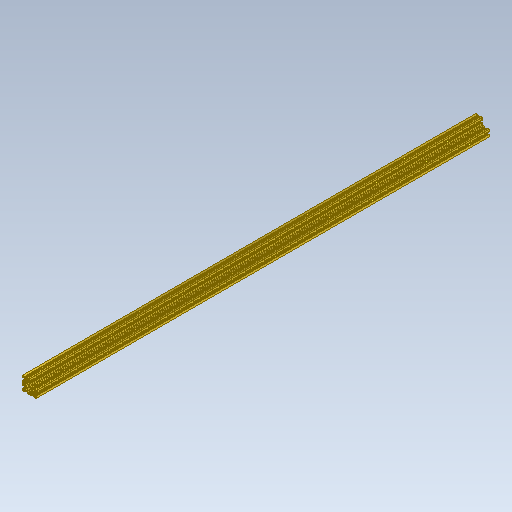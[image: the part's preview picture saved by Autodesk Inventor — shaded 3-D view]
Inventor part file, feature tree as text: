
AUTODESK INVENTOR PART (.ipt)
format: ipt  version: 2025.2 (Build 292293000, 293)  size: 549,376 bytes
history: native  units: mm
features: sketch x4, extrude x1, fillet x1
ambient origin geometry x8: Origin, YZ Plane, XZ Plane, XY Plane, X Axis, Y Axis, Z Axis, Center Point
bodies: Body1 (feature_tree)
feature tree (6):
  extrude  "Extrusão2"  Depth=10.0mm
  fillet  "Arredondamento1"  Radius=10.0mm
  sketch  "Esboço1"  dims[d0=60.0mm d3=15.0mm d4=10.0mm]
  sketch  "Esboço - Padrão circular1"  dims[d5=26.5mm]
  sketch  "Esboço - Padrão circular2"  dims[d7=4.5mm]
  sketch  "Esboço - Padrão circular3"  dims[d9=8.0mm d10=8.2mm d14=1.1mm d16=1.1mm d18=1.1mm d20=2.2mm d21=2.2mm d22=40.0mm d24=360.0deg d27=8.0mm d30=40.0mm d32=360.0deg d34=1.1mm d35=1.1mm d36=2.2mm d37=2.2mm d41=8.0mm d43=40.0mm d45=360.0deg d47=2000.0mm d48=0.0mm d49=1.0mm d23=0.5mm]
